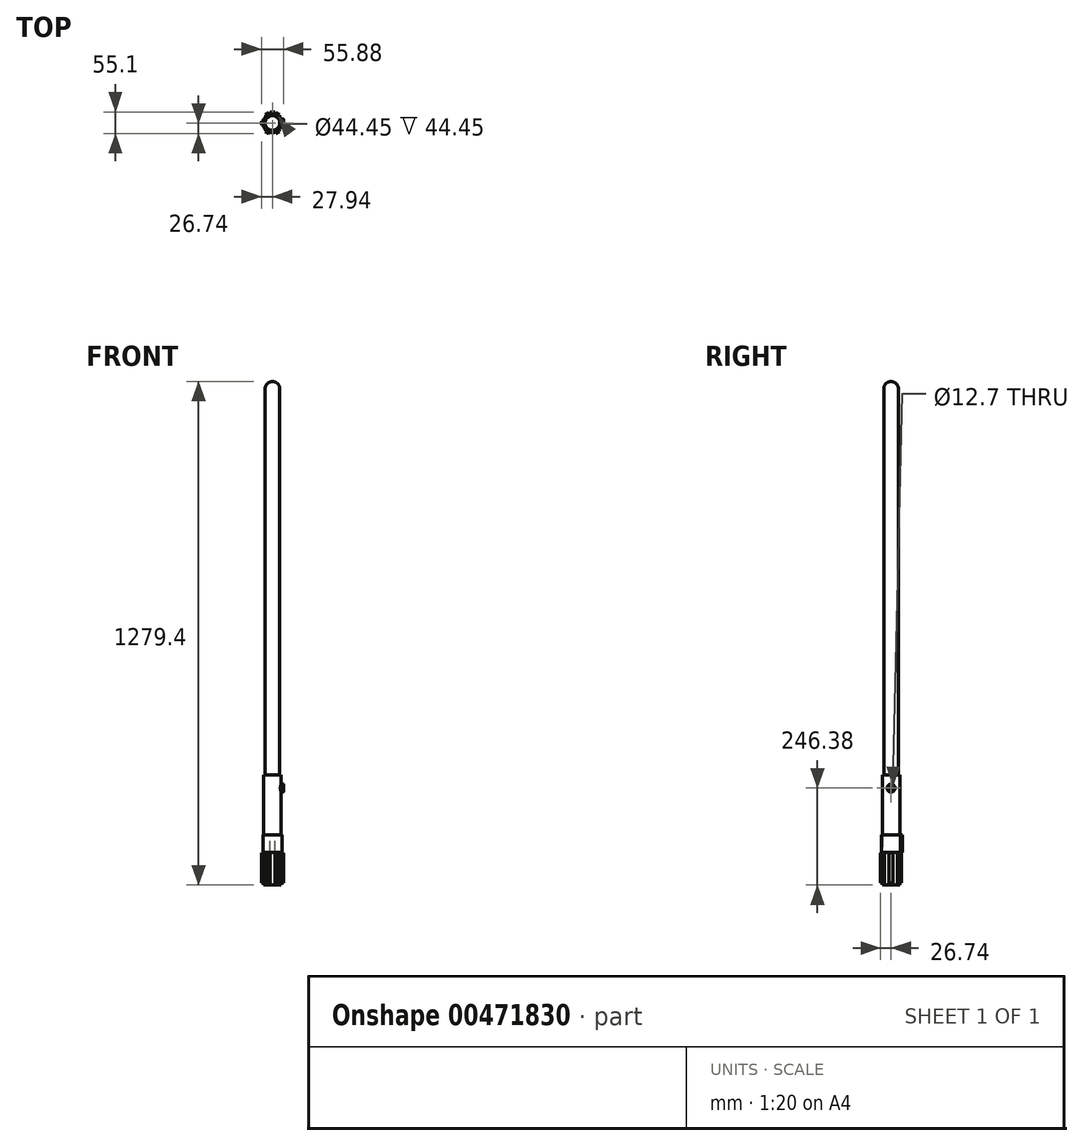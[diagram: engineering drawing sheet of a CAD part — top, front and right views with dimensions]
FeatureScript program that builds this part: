
annotation { "Feature Type Name" : "Feature", "Feature Type Description" : "" }
export const myFeature = defineFeature(function(context is Context, id is Id, definition is map)
    precondition{}
    {
        {
            var Q0;
            Q0=qCreatedBy(makeId("Right.planeOp"),FACE);
            cPlane(context, id + "F0", {"entities" : qUnion([Q0]), "cplaneType" : CPlaneType.OFFSET, "offset" : 27.94 * mm, "width" : 152.4 * mm, "height" : 152.4 * mm});
        }
        {
            var Q0;
            Q0=qCreatedBy(makeId("Top.planeOp"),FACE);
            cPlane(context, id + "F1", {"entities" : qUnion([Q0]), "cplaneType" : CPlaneType.OFFSET, "offset" : 12.7 * mm, "oppositeDirection" : true, "width" : 152.4 * mm, "height" : 152.4 * mm});
        }
        {
            var Q0;
            Q0=qCreatedBy(makeId("Top.planeOp"),FACE);
            var sketch = newSketch(context, id + "F2", { "sketchPlane" : qUnion([Q0])});
            skCircle(sketch, "E0", {"center": v(0, 0) * mm, "radius": 22.23 * mm});
            skSolve(sketch);
        }
        {
            var Q0;
            Q0 = qSketchRegion(id + "F2", true);
            extrude(context, id + "F3", {"entities" : qUnion([Q0]), "endBound" : BoundingType.SYMMETRIC, "depth" : 279.4 * mm});
        }
        {
            var Q0;
            Q0=qCreatedBy(id+"F0.planeOp",FACE);
            var sketch = newSketch(context, id + "F4", { "sketchPlane" : qUnion([Q0])});
            skLineSegment(sketch, "E1.bottom", {"start": v(-5.08, -134.62) * mm, "end": v(5.08, -134.62) * mm});
            skLineSegment(sketch, "E1.top", {"start": v(-5.08, -58.42) * mm, "end": v(5.08, -58.42) * mm});
            skLineSegment(sketch, "E1.left", {"start": v(-5.08, -134.62) * mm, "end": v(-5.08, -58.42) * mm});
            skLineSegment(sketch, "E1.right", {"start": v(5.08, -134.62) * mm, "end": v(5.08, -58.42) * mm});
            skSolve(sketch);
        }
        {
            var Q0;
            Q0 = qSketchRegion(id + "F4", true);
            var Q1;
            Q1=makeQuery(id+"F3.opExtrude","SWEPT_FACE",FACE,{"disambiguationData":[OSD([sQuery(id+"F2.wireOp",EDGE,"E0")])]});
            extrude(context, id + "F5", {"entities" : qUnion([Q0]), "endBound" : BoundingType.UP_TO_SURFACE, "oppositeDirection" : true, "endBoundEntityFace" : qUnion([Q1]), "depth" : 25.4 * mm});
        }
        {
            var Q0;
            Q0=qCreatedBy(makeId("Right.planeOp"),FACE);
            var sketch = newSketch(context, id + "F6", { "sketchPlane" : qUnion([Q0])});
            skLineSegment(sketch, "E2", {"start": v(0, 53.57) * mm, "end": v(0, 0) * mm});
            skSolve(sketch);
        }
        {
            var Q0;
            Q0=makeQuery(id+"F5.opExtrude","SWEPT_BODY",BODY,{"disambiguationData":[OSD([sQuery(id+"F4.wireOp",EDGE,"E1.bottom"),sQuery(id+"F4.wireOp",EDGE,"E1.top"),sQuery(id+"F4.wireOp",EDGE,"E1.left"),sQuery(id+"F4.wireOp",EDGE,"E1.right")])]});
            var Q1;
            Q1=sQuery(id+"F6.wireOp",EDGE,"E2");
            circularPattern(context, id + "F7", {"entities" : qUnion([Q0]), "axis" : qUnion([Q1]), "angle" : 360 * degree, "instanceCount" : 6, "equalSpace" : true});
        }
        {
            var Q0;
            Q0=qCreatedBy(id+"F1.planeOp",FACE);
            var sketch = newSketch(context, id + "F8", { "sketchPlane" : qUnion([Q0])});
            skCircle(sketch, "E3", {"center": v(0, 0) * mm, "radius": 22.23 * mm});
            skArc(sketch, "E4", {"start": v(-6.35, 23.28) * mm, "mid": v(0, -24.13) * mm, "end": v(6.35, 23.28) * mm});
            skLineSegment(sketch, "E5.top", {"start": v(6.35, 28.36) * mm, "end": v(-6.35, 28.36) * mm});
            skLineSegment(sketch, "E5.left", {"start": v(6.35, 23.28) * mm, "end": v(6.35, 28.36) * mm});
            skLineSegment(sketch, "E5.right", {"start": v(-6.35, 23.28) * mm, "end": v(-6.35, 28.36) * mm});
            skSolve(sketch);
        }
        {
            var Q0;
            Q0 = qSketchRegion(id + "F8", true);
            extrude(context, id + "F9", {"entities" : qUnion([Q0]), "oppositeDirection" : true, "depth" : 44.45 * mm});
        }
        {
            var Q0;
            Q0=qCreatedBy(id+"F0.planeOp",FACE);
            var sketch = newSketch(context, id + "F10", { "sketchPlane" : qUnion([Q0])});
            skCircle(sketch, "E6", {"center": v(0, 106.68) * mm, "radius": 6.35 * mm});
            skCircle(sketch, "E7", {"center": v(0, 106.68) * mm, "radius": 10.16 * mm});
            skSolve(sketch);
        }
        {
            var Q0;
            Q0 = qSketchRegion(id + "F10", true);
            var Q1;
            Q1=makeQuery(id+"F3.opExtrude","SWEPT_FACE",FACE,{"disambiguationData":[OSD([sQuery(id+"F2.wireOp",EDGE,"E0")])]});
            extrude(context, id + "F11", {"entities" : qUnion([Q0]), "endBound" : BoundingType.UP_TO_SURFACE, "oppositeDirection" : true, "endBoundEntityFace" : qUnion([Q1]), "depth" : 25.4 * mm});
        }
        {
            var Q0;
            Q0=makeQuery(id+"F11.opExtrude","CAP_EDGE",EDGE,{"disambiguationData":[OSD([sQuery(id+"F10.wireOp",EDGE,"E6")])],"isStart":true});
            chamfer(context, id + "F12", {"entities" : qUnion([Q0]), "width" : 2.54 * mm, "tangentPropagation" : true});
        }
        {
            var Q0;
            Q0=makeQuery(id+"F12.opChamfer","BLEND_FACE",FACE,{"disambiguationData":[OSD([sQuery(id+"F10.wireOp",EDGE,"E6")])]});
            var Q1;
            Q1=makeQuery(id+"F11.opExtrude","CAP_EDGE",EDGE,{"disambiguationData":[OSD([sQuery(id+"F10.wireOp",EDGE,"E7")])],"isStart":true});
            fillet(context, id + "F13", {"entities" : qUnion([Q0, Q1]), "radius" : 0.76 * mm, "tangentPropagation" : true, "allowEdgeOverflow" : false});
        }
        {
            var Q0;
            Q0=qCreatedBy(id+"F0.planeOp",FACE);
            var sketch = newSketch(context, id + "F14", { "sketchPlane" : qUnion([Q0])});
            skCircle(sketch, "E8", {"center": v(0, 106.68) * mm, "radius": 5.72 * mm});
            skSolve(sketch);
        }
        {
            var Q0;
            Q0 = qSketchRegion(id + "F14", true);
            var Q1;
            Q1=makeQuery(id+"F3.opExtrude","SWEPT_FACE",FACE,{"disambiguationData":[OSD([sQuery(id+"F2.wireOp",EDGE,"E0")])]});
            extrude(context, id + "F15", {"entities" : qUnion([Q0]), "endBound" : BoundingType.UP_TO_SURFACE, "oppositeDirection" : true, "endBoundEntityFace" : qUnion([Q1]), "depth" : 25.4 * mm});
        }
        {
            var Q0;
            Q0=makeQuery(id+"F15.opExtrude","CAP_FACE",FACE,{"disambiguationData":[OSD([sQuery(id+"F14.wireOp",EDGE,"E8")])],"isStart":true});
            fillet(context, id + "F16", {"entities" : qUnion([Q0]), "radius" : 0.5 * mm, "tangentPropagation" : true, "allowEdgeOverflow" : false});
        }
        {
            var Q0;
            Q0=makeQuery(id+"F3.opExtrude","CAP_FACE",FACE,{"disambiguationData":[OSD([sQuery(id+"F2.wireOp",EDGE,"E0")])],"isStart":false});
            var sketch = newSketch(context, id + "F17", { "sketchPlane" : qUnion([Q0])});
            skCircle(sketch, "E9", {"center": v(0, 0) * mm, "radius": 18.67 * mm});
            skSolve(sketch);
        }
        {
            var Q0;
            Q0 = qSketchRegion(id + "F17", true);
            extrude(context, id + "F18", {"entities" : qUnion([Q0]), "depth" : 1000 * mm});
        }
        {
            var Q0;
            Q0=makeQuery(id+"F18.opExtrude","CAP_EDGE",EDGE,{"disambiguationData":[OSD([sQuery(id+"F17.wireOp",EDGE,"E9")])],"isStart":false});
            fillet(context, id + "F19", {"entities" : qUnion([Q0]), "radius" : 18.29 * mm, "tangentPropagation" : true, "allowEdgeOverflow" : false});
        }
    });
